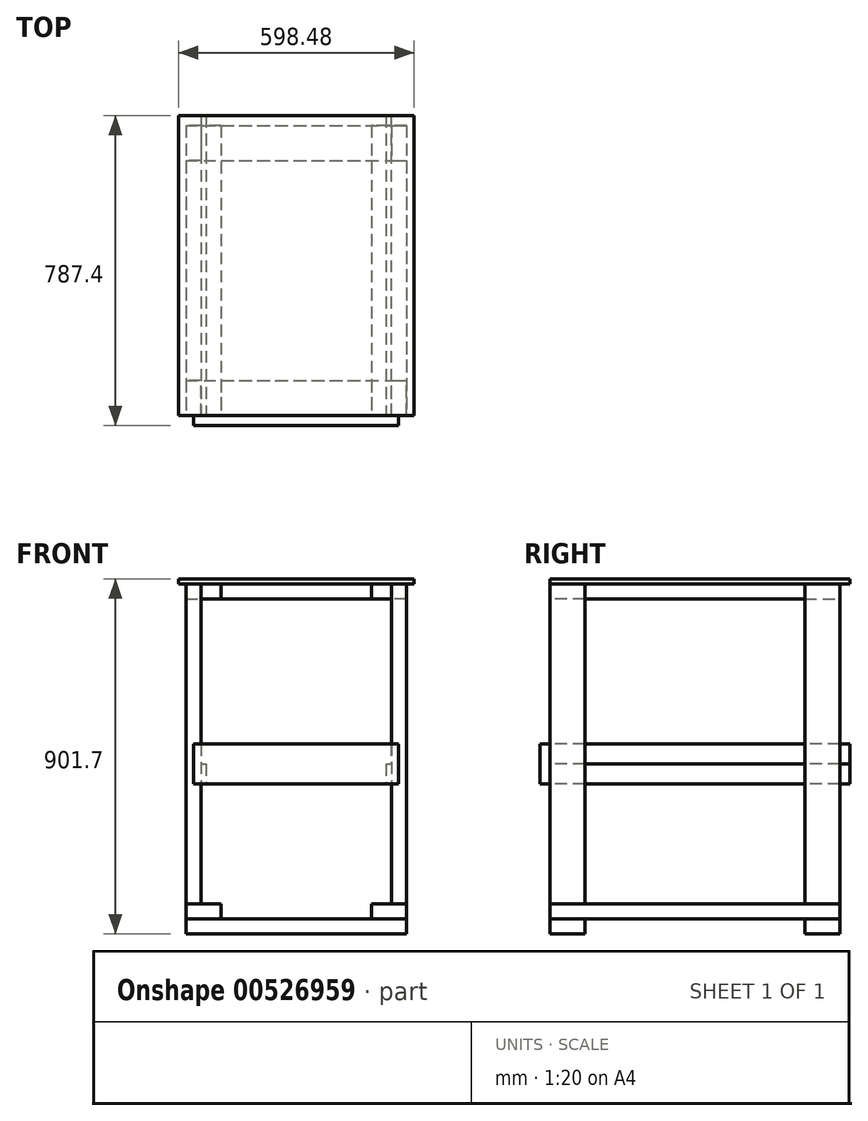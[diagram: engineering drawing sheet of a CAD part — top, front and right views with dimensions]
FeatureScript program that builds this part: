
annotation { "Feature Type Name" : "Feature", "Feature Type Description" : "" }
export const myFeature = defineFeature(function(context is Context, id is Id, definition is map)
    precondition{}
    {
        {
            var Q0;
            Q0=qCreatedBy(makeId("Front.planeOp"),FACE);
            var sketch = newSketch(context, id + "F0", { "sketchPlane" : qUnion([Q0])});
            skLineSegment(sketch, "E0.bottom", {"start": v(228.6, 50.8) * mm, "end": v(-228.6, 50.8) * mm});
            skLineSegment(sketch, "E0.top", {"start": v(228.6, -50.8) * mm, "end": v(-228.6, -50.8) * mm});
            skLineSegment(sketch, "E0.left", {"start": v(228.6, 50.8) * mm, "end": v(228.6, -50.8) * mm});
            skLineSegment(sketch, "E0.right", {"start": v(-228.6, 50.8) * mm, "end": v(-228.6, -50.8) * mm});
            skPoint(sketch, "E0.middle", {"position": v(0, 0) * mm});
            skLineSegment(sketch, "E1.bottom", {"start": v(-241.3, 50.8) * mm, "end": v(241.3, 50.8) * mm});
            skLineSegment(sketch, "E1.top", {"start": v(-241.3, 0) * mm, "end": v(241.3, 0) * mm});
            skLineSegment(sketch, "E1.left", {"start": v(-241.3, 50.8) * mm, "end": v(-241.3, 0) * mm});
            skLineSegment(sketch, "E1.right", {"start": v(241.3, 50.8) * mm, "end": v(241.3, 0) * mm});
            skLineSegment(sketch, "E2", {"start": v(228.6, -50.8) * mm, "end": v(241.3, 0) * mm, "construction": true});
            skLineSegment(sketch, "E3", {"start": v(-241.3, 0) * mm, "end": v(-228.6, -50.8) * mm, "construction": true});
            skSolve(sketch);
        }
        {
            var Q0;
            Q0 = qSketchRegion(id + "F0", true);
            extrude(context, id + "F1", {"entities" : qUnion([Q0]), "oppositeDirection" : true, "depth" : 762 * mm, "offsetDistance" : 25.4 * mm});
        }
        {
            var Q0;
            Q0=makeQuery(id+"F1.opExtrude","CAP_FACE",FACE,{"disambiguationData":[OSD([sQuery(id+"F0.wireOp",EDGE,"E0.top"),sQuery(id+"F0.wireOp",EDGE,"E0.left"),sQuery(id+"F0.wireOp",EDGE,"E0.right"),sQuery(id+"F0.wireOp",EDGE,"E1.bottom"),sQuery(id+"F0.wireOp",EDGE,"E1.top"),sQuery(id+"F0.wireOp",EDGE,"E1.left"),sQuery(id+"F0.wireOp",EDGE,"E1.right")])],"isStart":true});
            var sketch = newSketch(context, id + "F2", { "sketchPlane" : qUnion([Q0])});
            skLineSegment(sketch, "E4.bottom", {"start": v(260.35, 50.8) * mm, "end": v(-260.35, 50.8) * mm});
            skLineSegment(sketch, "E4.top", {"start": v(260.35, -50.8) * mm, "end": v(-260.35, -50.8) * mm});
            skLineSegment(sketch, "E4.left", {"start": v(260.35, 50.8) * mm, "end": v(260.35, -50.8) * mm});
            skLineSegment(sketch, "E4.right", {"start": v(-260.35, 50.8) * mm, "end": v(-260.35, -50.8) * mm});
            skPoint(sketch, "E4.middle", {"position": v(0, 0) * mm});
            skSolve(sketch);
        }
        {
            var Q0;
            Q0 = qSketchRegion(id + "F2", true);
            extrude(context, id + "F3", {"entities" : qUnion([Q0]), "operationType" : NewBodyOperationType.ADD, "depth" : 25.4 * mm, "offsetDistance" : 25.4 * mm});
        }
        {
            var Q0;
            Q0=makeQuery(id+"F3.boolean.opBoolean","MERGE",FACE,{"derivedFrom":[makeQuery(id+"F1.opExtrude","SWEPT_FACE",FACE,{"disambiguationData":[OSD([sQuery(id+"F0.wireOp",EDGE,"E1.bottom")])]}),makeQuery(id+"F3.opExtrude","SWEPT_FACE",FACE,{"disambiguationData":[OSD([sQuery(id+"F2.wireOp",EDGE,"E4.bottom")])]})]});
            var sketch = newSketch(context, id + "F4", { "sketchPlane" : qUnion([Q0])});
            skLineSegment(sketch, "E5.bottom", {"start": v(-242.1, 0) * mm, "end": v(-280.2, 0) * mm});
            skLineSegment(sketch, "E5.top", {"start": v(-242.1, 88.9) * mm, "end": v(-280.2, 88.9) * mm});
            skLineSegment(sketch, "E5.left", {"start": v(-242.1, 0) * mm, "end": v(-242.1, 88.9) * mm});
            skLineSegment(sketch, "E5.right", {"start": v(-280.2, 0) * mm, "end": v(-280.2, 88.9) * mm});
            skLineSegment(sketch, "E6.bottom", {"start": v(-242.1, 736.6) * mm, "end": v(-280.2, 736.6) * mm});
            skLineSegment(sketch, "E6.top", {"start": v(-242.1, 647.7) * mm, "end": v(-280.2, 647.7) * mm});
            skLineSegment(sketch, "E6.left", {"start": v(-242.1, 736.6) * mm, "end": v(-242.1, 647.7) * mm});
            skLineSegment(sketch, "E6.right", {"start": v(-280.2, 736.6) * mm, "end": v(-280.2, 647.7) * mm});
            skLineSegment(sketch, "E7", {"start": v(-242.1, 647.7) * mm, "end": v(-242.1, 88.9) * mm, "construction": true});
            skLineSegment(sketch, "E8", {"start": v(0, 0) * mm, "end": v(0, 957.3) * mm, "construction": true});
            skPoint(sketch, "E8.endSnap0", {"position": v(0, 762) * mm});
            skLineSegment(sketch, "E9.MirrorCS", {"start": v(242.1, 736.6) * mm, "end": v(280.2, 736.6) * mm});
            skLineSegment(sketch, "E10.MirrorCS", {"start": v(280.2, 736.6) * mm, "end": v(280.2, 647.7) * mm});
            skLineSegment(sketch, "E11.MirrorCS", {"start": v(242.1, 736.6) * mm, "end": v(242.1, 647.7) * mm});
            skLineSegment(sketch, "E12.MirrorCS", {"start": v(242.1, 647.7) * mm, "end": v(280.2, 647.7) * mm});
            skLineSegment(sketch, "E13.MirrorCS", {"start": v(242.1, 88.9) * mm, "end": v(280.2, 88.9) * mm});
            skLineSegment(sketch, "E14.MirrorCS", {"start": v(280.2, 0) * mm, "end": v(280.2, 88.9) * mm});
            skLineSegment(sketch, "E15.MirrorCS", {"start": v(242.1, 0) * mm, "end": v(280.2, 0) * mm});
            skLineSegment(sketch, "E16.MirrorCS", {"start": v(242.1, 0) * mm, "end": v(242.1, 88.9) * mm});
            skSolve(sketch);
        }
        {
            var Q0;
            Q0 = qSketchRegion(id + "F4", true);
            extrude(context, id + "F5", {"entities" : qUnion([Q0]), "endBound" : BoundingType.SYMMETRIC, "depth" : 812.8 * mm, "offsetDistance" : 25.4 * mm});
        }
        {
            var Q0;
            Q0=makeQuery(id+"F5.opExtrude","SWEPT_FACE",FACE,{"disambiguationData":[OSD([sQuery(id+"F4.wireOp",EDGE,"E5.bottom")])]});
            var sketch = newSketch(context, id + "F6", { "sketchPlane" : qUnion([Q0])});
            skLineSegment(sketch, "E17.0.0", {"start": v(242.1, -355.6) * mm, "end": v(280.2, -355.6) * mm, "construction": true});
            skLineSegment(sketch, "E17.0.1", {"start": v(280.2, -355.6) * mm, "end": v(280.2, 457.2) * mm, "construction": true});
            skLineSegment(sketch, "E17.0.2", {"start": v(280.2, 457.2) * mm, "end": v(242.1, 457.2) * mm, "construction": true});
            skLineSegment(sketch, "E17.0.3", {"start": v(242.1, 457.2) * mm, "end": v(242.1, -355.6) * mm, "construction": true});
            skLineSegment(sketch, "E18.bottom", {"start": v(-280.2, -355.6) * mm, "end": v(-191.3, -355.6) * mm});
            skLineSegment(sketch, "E18.top", {"start": v(-280.2, -393.7) * mm, "end": v(-191.3, -393.7) * mm});
            skLineSegment(sketch, "E18.left", {"start": v(-280.2, -355.6) * mm, "end": v(-280.2, -393.7) * mm});
            skLineSegment(sketch, "E18.right", {"start": v(-191.3, -355.6) * mm, "end": v(-191.3, -393.7) * mm});
            skLineSegment(sketch, "E19", {"start": v(0, 0) * mm, "end": v(0, -471.75) * mm, "construction": true});
            skLineSegment(sketch, "E20.MirrorCS", {"start": v(280.2, -355.6) * mm, "end": v(191.3, -355.6) * mm});
            skLineSegment(sketch, "E21.MirrorCS", {"start": v(280.2, -355.6) * mm, "end": v(280.2, -393.7) * mm});
            skLineSegment(sketch, "E22.MirrorCS", {"start": v(280.2, -393.7) * mm, "end": v(191.3, -393.7) * mm});
            skLineSegment(sketch, "E23.MirrorCS", {"start": v(191.3, -355.6) * mm, "end": v(191.3, -393.7) * mm});
            skSolve(sketch);
        }
        {
            var Q0;
            Q0 = qSketchRegion(id + "F6", true);
            var Q1;
            Q1=makeQuery(id+"F5.opExtrude","CAP_VERTEX",VERTEX,{"disambiguationData":[OSD([sQuery(id+"F4.wireOp",EDGE,"E9.MirrorCS"),sQuery(id+"F4.wireOp",EDGE,"E10.MirrorCS")])],"isStart":true});
            extrude(context, id + "F7", {"entities" : qUnion([Q0]), "endBound" : BoundingType.UP_TO_VERTEX, "oppositeDirection" : true, "depth" : 25.4 * mm, "endBoundEntityVertex" : qUnion([Q1]), "offsetDistance" : 25.4 * mm});
        }
        {
            var Q0;
            Q0=makeQuery(id+"F7.opExtrude","SWEPT_FACE",FACE,{"disambiguationData":[OSD([sQuery(id+"F6.wireOp",EDGE,"E21.MirrorCS")])]});
            var sketch = newSketch(context, id + "F8", { "sketchPlane" : qUnion([Q0])});
            skLineSegment(sketch, "E24.bottom", {"start": v(0, -393.7) * mm, "end": v(88.9, -393.7) * mm});
            skLineSegment(sketch, "E24.top", {"start": v(0, -431.8) * mm, "end": v(88.9, -431.8) * mm});
            skLineSegment(sketch, "E24.left", {"start": v(0, -393.7) * mm, "end": v(0, -431.8) * mm});
            skLineSegment(sketch, "E24.right", {"start": v(88.9, -393.7) * mm, "end": v(88.9, -431.8) * mm});
            skLineSegment(sketch, "E25", {"start": v(368.3, -355.6) * mm, "end": v(368.3, -393.7) * mm, "construction": true});
            skLineSegment(sketch, "E26.MirrorCS", {"start": v(647.7, -393.7) * mm, "end": v(647.7, -431.8) * mm});
            skLineSegment(sketch, "E27.MirrorCS", {"start": v(736.6, -393.7) * mm, "end": v(647.7, -393.7) * mm});
            skLineSegment(sketch, "E28.MirrorCS", {"start": v(736.6, -431.8) * mm, "end": v(647.7, -431.8) * mm});
            skLineSegment(sketch, "E29.MirrorCS", {"start": v(736.6, -393.7) * mm, "end": v(736.6, -431.8) * mm});
            skSolve(sketch);
        }
        {
            var Q0;
            Q0 = qSketchRegion(id + "F8", true);
            var Q1;
            Q1=makeQuery(id+"F7.opExtrude","CAP_VERTEX",VERTEX,{"disambiguationData":[OSD([sQuery(id+"F6.wireOp",EDGE,"E18.top"),sQuery(id+"F6.wireOp",EDGE,"E18.left")])],"isStart":true});
            extrude(context, id + "F9", {"entities" : qUnion([Q0]), "endBound" : BoundingType.UP_TO_VERTEX, "oppositeDirection" : true, "depth" : 25.4 * mm, "endBoundEntityVertex" : qUnion([Q1]), "offsetDistance" : 25.4 * mm});
        }
        {
            var Q0;
            Q0=makeQuery(id+"F5.opExtrude","CAP_FACE",FACE,{"disambiguationData":[OSD([sQuery(id+"F4.wireOp",EDGE,"E5.bottom"),sQuery(id+"F4.wireOp",EDGE,"E5.top"),sQuery(id+"F4.wireOp",EDGE,"E5.left"),sQuery(id+"F4.wireOp",EDGE,"E5.right")])],"isStart":false});
            var sketch = newSketch(context, id + "F10", { "sketchPlane" : qUnion([Q0])});
            skLineSegment(sketch, "E30.0.0", {"start": v(-280.2, 647.7) * mm, "end": v(-242.1, 647.7) * mm});
            skLineSegment(sketch, "E30.0.1", {"start": v(-242.1, 647.7) * mm, "end": v(-242.1, 736.6) * mm});
            skLineSegment(sketch, "E30.0.2", {"start": v(-242.1, 736.6) * mm, "end": v(-280.2, 736.6) * mm});
            skLineSegment(sketch, "E30.0.3", {"start": v(-280.2, 736.6) * mm, "end": v(-280.2, 647.7) * mm});
            skLineSegment(sketch, "E31.0.0", {"start": v(242.1, 736.6) * mm, "end": v(242.1, 647.7) * mm});
            skLineSegment(sketch, "E31.0.1", {"start": v(242.1, 647.7) * mm, "end": v(280.2, 647.7) * mm});
            skLineSegment(sketch, "E31.0.2", {"start": v(280.2, 647.7) * mm, "end": v(280.2, 736.6) * mm});
            skLineSegment(sketch, "E31.0.3", {"start": v(280.2, 736.6) * mm, "end": v(242.1, 736.6) * mm});
            skLineSegment(sketch, "E32.0.0", {"start": v(242.1, 88.9) * mm, "end": v(242.1, 0) * mm});
            skLineSegment(sketch, "E32.0.1", {"start": v(242.1, 0) * mm, "end": v(280.2, 0) * mm});
            skLineSegment(sketch, "E32.0.2", {"start": v(280.2, 0) * mm, "end": v(280.2, 88.9) * mm});
            skLineSegment(sketch, "E32.0.3", {"start": v(280.2, 88.9) * mm, "end": v(242.1, 88.9) * mm});
            skLineSegment(sketch, "E33.bottom", {"start": v(-280.2, 736.6) * mm, "end": v(-191.3, 736.6) * mm});
            skLineSegment(sketch, "E33.top", {"start": v(-280.2, 0) * mm, "end": v(-191.3, 0) * mm});
            skLineSegment(sketch, "E33.left", {"start": v(-280.2, 736.6) * mm, "end": v(-280.2, 0) * mm});
            skLineSegment(sketch, "E33.right", {"start": v(-191.3, 736.6) * mm, "end": v(-191.3, 0) * mm});
            skLineSegment(sketch, "E34.bottom", {"start": v(280.2, 736.6) * mm, "end": v(191.3, 736.6) * mm});
            skLineSegment(sketch, "E34.top", {"start": v(280.2, 0) * mm, "end": v(191.3, 0) * mm});
            skLineSegment(sketch, "E34.left", {"start": v(280.2, 736.6) * mm, "end": v(280.2, 0) * mm});
            skLineSegment(sketch, "E34.right", {"start": v(191.3, 736.6) * mm, "end": v(191.3, 0) * mm});
            skLineSegment(sketch, "E35.bottom", {"start": v(-191.3, 736.6) * mm, "end": v(191.3, 736.6) * mm});
            skLineSegment(sketch, "E35.top", {"start": v(-191.3, 647.7) * mm, "end": v(191.3, 647.7) * mm});
            skLineSegment(sketch, "E35.left", {"start": v(-191.3, 736.6) * mm, "end": v(-191.3, 647.7) * mm});
            skLineSegment(sketch, "E35.right", {"start": v(191.3, 736.6) * mm, "end": v(191.3, 647.7) * mm});
            skLineSegment(sketch, "E36.bottom", {"start": v(-191.3, 0) * mm, "end": v(191.3, 0) * mm});
            skLineSegment(sketch, "E36.top", {"start": v(-191.3, 88.9) * mm, "end": v(191.3, 88.9) * mm});
            skLineSegment(sketch, "E36.left", {"start": v(-191.3, 0) * mm, "end": v(-191.3, 88.9) * mm});
            skLineSegment(sketch, "E36.right", {"start": v(191.3, 0) * mm, "end": v(191.3, 88.9) * mm});
            skSolve(sketch);
        }
        {
            var Q0;
            {var subQ7=sQuery(id+"F10.wireOp",EDGE,"E30.0.0");Q0=makeQuery(id+"F10.imprint","IMPRINT",FACE,{"disambiguationData":[TD([[makeQuery(id+"F10.imprint","IMPRINT",EDGE,{"derivedFrom":subQ7}),-1.0]])]});}
            var Q1;
            {var subQ3=sQuery(id+"F10.wireOp",EDGE,"E31.0.0");Q1=makeQuery(id+"F10.imprint","IMPRINT",FACE,{"disambiguationData":[TD([[makeQuery(id+"F10.imprint","IMPRINT",EDGE,{"derivedFrom":subQ3}),-1.0]])]});}
            extrude(context, id + "F11", {"entities" : qUnion([Q0, Q1]), "oppositeDirection" : true, "depth" : 38.1 * mm, "offsetDistance" : 25.4 * mm});
        }
        {
            var Q0;
            Q0=makeQuery(id+"F10.imprint","IMPRINT",FACE,{"disambiguationData":[TD([[makeQuery(id+"F10.imprint","IMPRINT",EDGE,{"derivedFrom":sQuery(id+"F10.wireOp",EDGE,"E35.bottom")}),-1.0]])]});
            var Q1;
            Q1=makeQuery(id+"F10.imprint","IMPRINT",FACE,{"disambiguationData":[TD([[makeQuery(id+"F10.imprint","IMPRINT",EDGE,{"derivedFrom":sQuery(id+"F10.wireOp",EDGE,"E36.bottom")}),1.0]])]});
            extrude(context, id + "F12", {"entities" : qUnion([Q0, Q1]), "oppositeDirection" : true, "depth" : 38.1 * mm, "offsetDistance" : 25.4 * mm});
        }
        {
            var Q0;
            Q0=makeQuery(id+"F5.opExtrude","SWEPT_FACE",FACE,{"disambiguationData":[OSD([sQuery(id+"F4.wireOp",EDGE,"E5.bottom")])]});
            var sketch = newSketch(context, id + "F13", { "sketchPlane" : qUnion([Q0])});
            skLineSegment(sketch, "E37.bottom", {"start": v(-299.24, 469.9) * mm, "end": v(299.24, 469.9) * mm});
            skLineSegment(sketch, "E37.top", {"start": v(-299.24, 457.2) * mm, "end": v(299.24, 457.2) * mm});
            skLineSegment(sketch, "E37.left", {"start": v(-299.24, 469.9) * mm, "end": v(-299.24, 457.2) * mm});
            skLineSegment(sketch, "E37.right", {"start": v(299.24, 469.9) * mm, "end": v(299.24, 457.2) * mm});
            skLineSegment(sketch, "E38", {"start": v(-299.24, 457.2) * mm, "end": v(-280.2, 457.2) * mm, "construction": true});
            skLineSegment(sketch, "E39.0.0", {"start": v(242.1, -355.6) * mm, "end": v(280.2, -355.6) * mm, "construction": true});
            skLineSegment(sketch, "E39.0.1", {"start": v(280.2, -355.6) * mm, "end": v(280.2, 457.2) * mm, "construction": true});
            skLineSegment(sketch, "E39.0.2", {"start": v(280.2, 457.2) * mm, "end": v(242.1, 457.2) * mm, "construction": true});
            skLineSegment(sketch, "E39.0.3", {"start": v(242.1, 457.2) * mm, "end": v(242.1, -355.6) * mm, "construction": true});
            skLineSegment(sketch, "E40", {"start": v(280.2, 457.2) * mm, "end": v(299.24, 457.2) * mm, "construction": true});
            skSolve(sketch);
        }
        {
            var Q0;
            Q0 = qSketchRegion(id + "F13", true);
            extrude(context, id + "F14", {"entities" : qUnion([Q0]), "oppositeDirection" : true, "depth" : 762 * mm, "offsetDistance" : 25.4 * mm});
        }
    });
